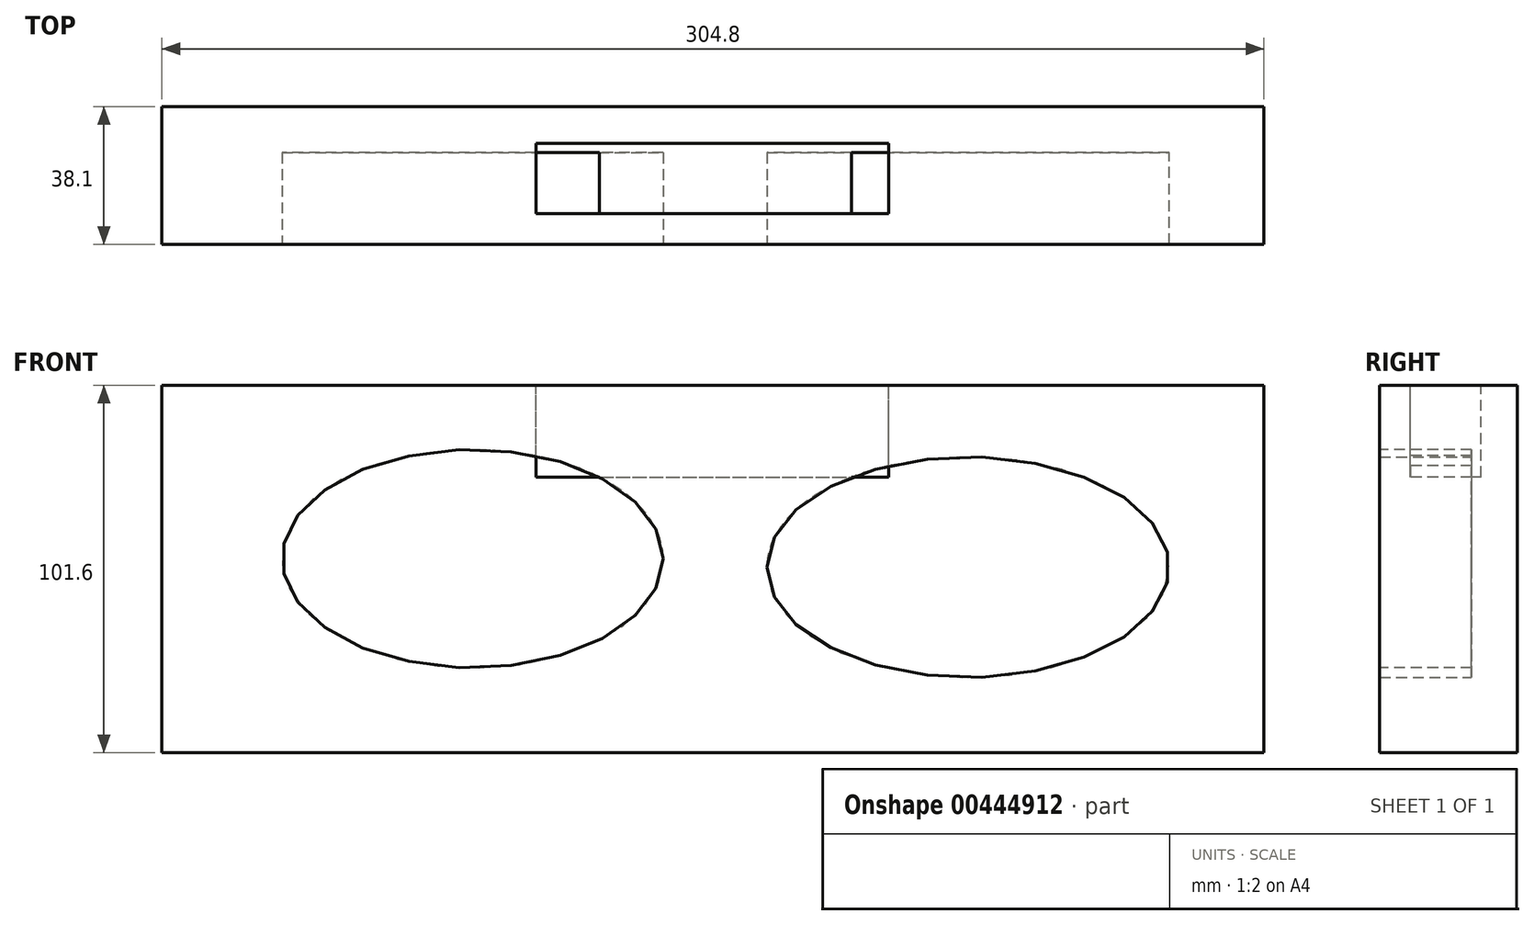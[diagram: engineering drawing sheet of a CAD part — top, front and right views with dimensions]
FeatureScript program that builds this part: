
annotation { "Feature Type Name" : "Feature", "Feature Type Description" : "" }
export const myFeature = defineFeature(function(context is Context, id is Id, definition is map)
    precondition{}
    {
        {
            var Q0;
            Q0=qCreatedBy(makeId("Front.planeOp"),FACE);
            var sketch = newSketch(context, id + "F0", { "sketchPlane" : qUnion([Q0])});
            skLineSegment(sketch, "E0.bottom", {"start": v(-235, 50.27) * mm, "end": v(69.8, 50.27) * mm});
            skLineSegment(sketch, "E0.top", {"start": v(-235, -51.33) * mm, "end": v(69.8, -51.33) * mm});
            skLineSegment(sketch, "E0.left", {"start": v(-235, 50.27) * mm, "end": v(-235, -51.33) * mm});
            skLineSegment(sketch, "E0.right", {"start": v(69.8, 50.27) * mm, "end": v(69.8, -51.33) * mm});
            skSolve(sketch);
        }
        {
            var Q0;
            Q0 = qSketchRegion(id + "F0", true);
            extrude(context, id + "F1", {"entities" : qUnion([Q0]), "depth" : 38.1 * mm});
        }
        {
            var Q0;
            Q0=makeQuery(id+"F1.opExtrude","CAP_FACE",FACE,{"disambiguationData":[OSD([sQuery(id+"F0.wireOp",EDGE,"E0.bottom"),sQuery(id+"F0.wireOp",EDGE,"E0.top"),sQuery(id+"F0.wireOp",EDGE,"E0.left"),sQuery(id+"F0.wireOp",EDGE,"E0.right")])],"isStart":false});
            var sketch = newSketch(context, id + "F2", { "sketchPlane" : qUnion([Q0])});
            skEllipse(sketch, "E1", {"center": v(-149.09, 2.34) * mm, "majorRadius": 52.7 * mm, "minorRadius": 30.18 * mm, "majorAxis": v(1, 0)});
            skSolve(sketch);
        }
        {
            var Q0;
            Q0 = qSketchRegion(id + "F2", true);
            extrude(context, id + "F3", {"entities" : qUnion([Q0]), "operationType" : NewBodyOperationType.REMOVE, "oppositeDirection" : true, "depth" : 25.4 * mm});
        }
        {
            var Q0;
            Q0=makeQuery(id+"F1.opExtrude","CAP_FACE",FACE,{"disambiguationData":[OSD([sQuery(id+"F0.wireOp",EDGE,"E0.bottom"),sQuery(id+"F0.wireOp",EDGE,"E0.top"),sQuery(id+"F0.wireOp",EDGE,"E0.left"),sQuery(id+"F0.wireOp",EDGE,"E0.right")])],"isStart":false});
            var sketch = newSketch(context, id + "F4", { "sketchPlane" : qUnion([Q0])});
            skEllipse(sketch, "E2", {"center": v(-12.06, 0) * mm, "majorRadius": 55.63 * mm, "minorRadius": 30.5 * mm, "majorAxis": v(-1, 0)});
            skSolve(sketch);
        }
        {
            var Q0;
            Q0 = qSketchRegion(id + "F4", true);
            extrude(context, id + "F5", {"entities" : qUnion([Q0]), "operationType" : NewBodyOperationType.REMOVE, "oppositeDirection" : true, "depth" : 25.4 * mm});
        }
        {
            var Q0;
            Q0=makeQuery(id+"F1.opExtrude","SWEPT_FACE",FACE,{"disambiguationData":[OSD([sQuery(id+"F0.wireOp",EDGE,"E0.bottom")])]});
            var sketch = newSketch(context, id + "F6", { "sketchPlane" : qUnion([Q0])});
            skLineSegment(sketch, "E3.bottom", {"start": v(-131.52, -10.1) * mm, "end": v(-34.02, -10.1) * mm});
            skLineSegment(sketch, "E3.top", {"start": v(-131.52, -29.56) * mm, "end": v(-34.02, -29.56) * mm});
            skLineSegment(sketch, "E3.left", {"start": v(-131.52, -10.1) * mm, "end": v(-131.52, -29.56) * mm});
            skLineSegment(sketch, "E3.right", {"start": v(-34.02, -10.1) * mm, "end": v(-34.02, -29.56) * mm});
            skSolve(sketch);
        }
        {
            var Q0;
            Q0 = qSketchRegion(id + "F6", true);
            extrude(context, id + "F7", {"entities" : qUnion([Q0]), "operationType" : NewBodyOperationType.REMOVE, "oppositeDirection" : true, "depth" : 25.4 * mm});
        }
    });
